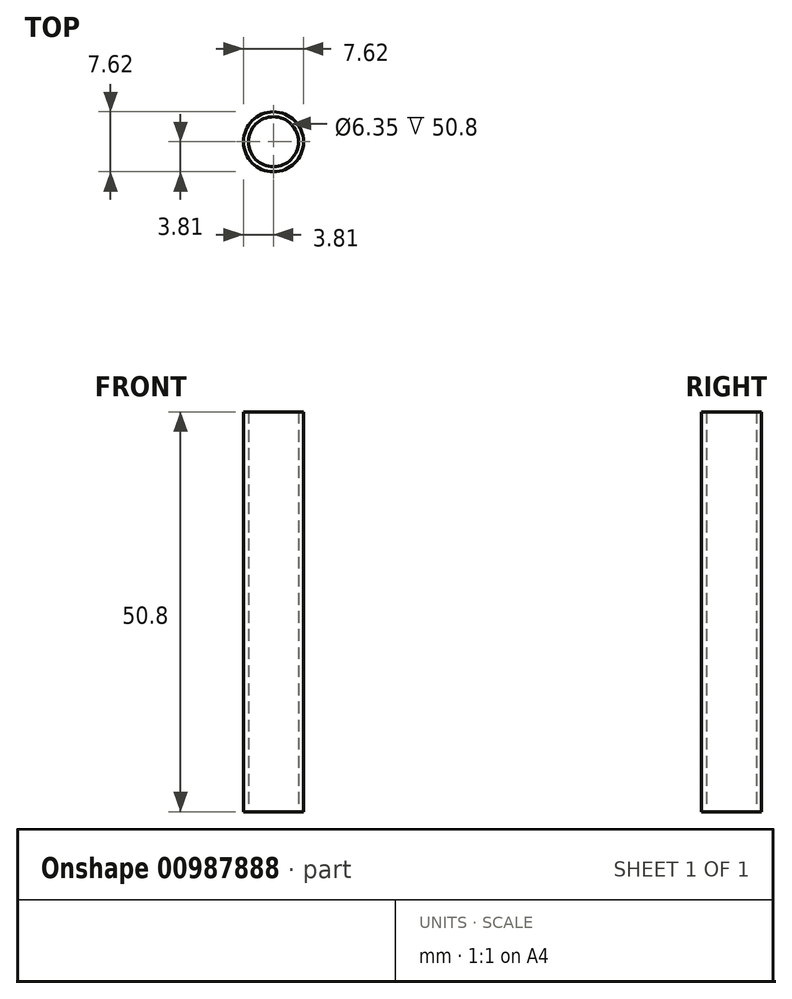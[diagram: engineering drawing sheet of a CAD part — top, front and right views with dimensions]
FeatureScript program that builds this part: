
annotation { "Feature Type Name" : "Feature", "Feature Type Description" : "" }
export const myFeature = defineFeature(function(context is Context, id is Id, definition is map)
    precondition{}
    {
        {
            var Q0;
            Q0=qCreatedBy(makeId("Top.planeOp"),FACE);
            var sketch = newSketch(context, id + "F0", { "sketchPlane" : qUnion([Q0])});
            skCircle(sketch, "E0", {"center": v(0, 0) * mm, "radius": 3.18 * mm});
            skCircle(sketch, "E1", {"center": v(0, 0) * mm, "radius": 3.81 * mm});
            skSolve(sketch);
        }
        {
            var Q0;
            Q0=makeQuery(id+"F0.imprint","IMPRINT",FACE,{"disambiguationData":[TD([[makeQuery(id+"F0.imprint","IMPRINT",EDGE,{"derivedFrom":sQuery(id+"F0.wireOp",EDGE,"E0")}),-1.0]])]});
            extrude(context, id + "F1", {"entities" : qUnion([Q0]), "depth" : 50.8 * mm, "offsetDistance" : 25.4 * mm});
        }
    });
